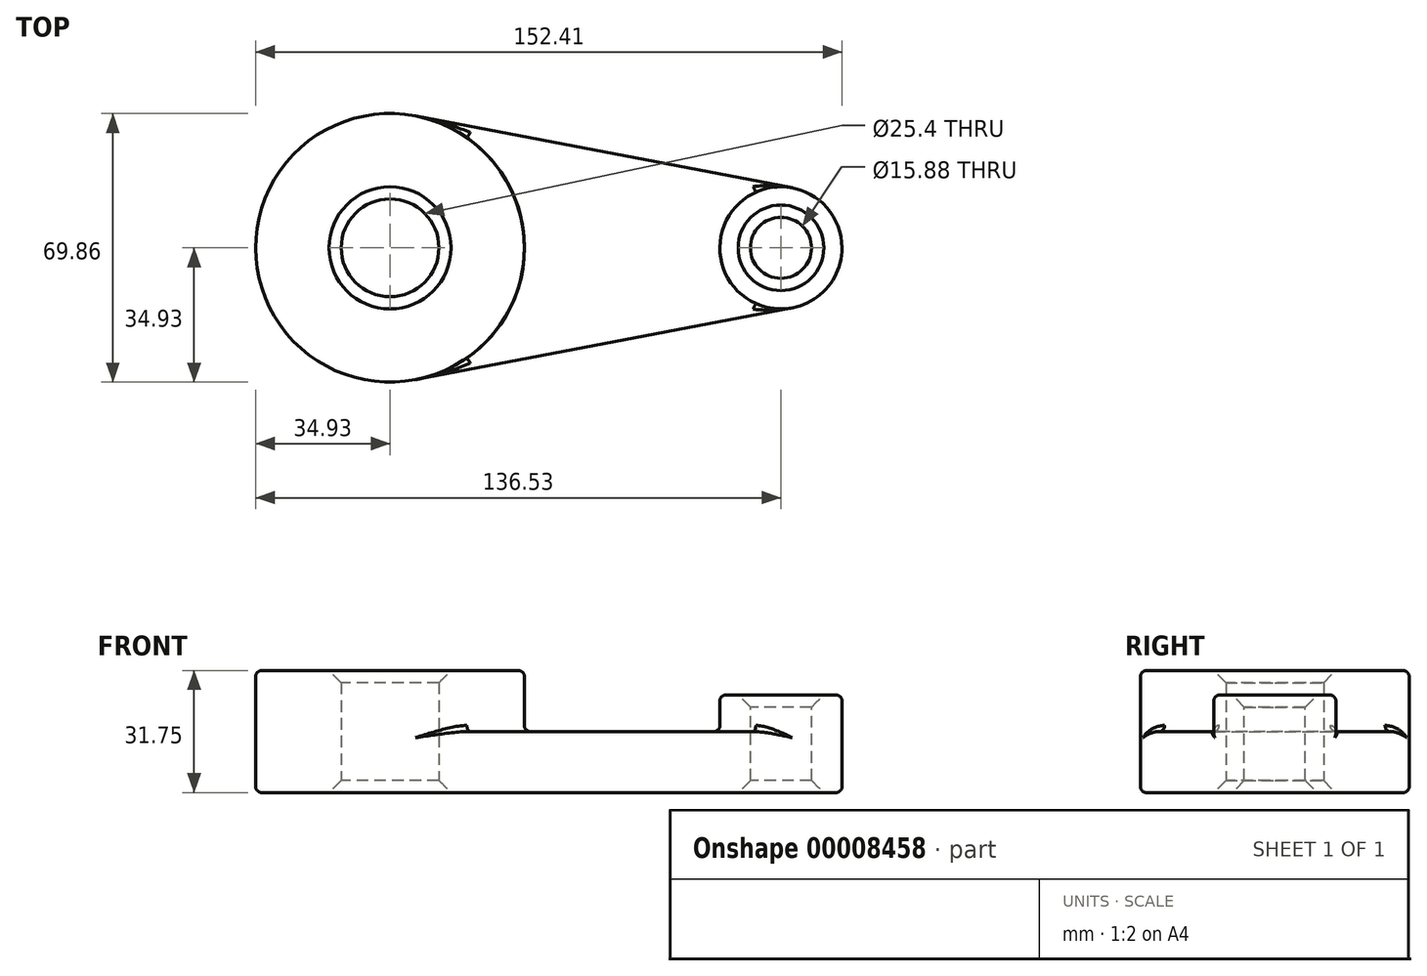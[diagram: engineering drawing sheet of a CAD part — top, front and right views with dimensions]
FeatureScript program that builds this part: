
annotation { "Feature Type Name" : "Feature", "Feature Type Description" : "" }
export const myFeature = defineFeature(function(context is Context, id is Id, definition is map)
    precondition{}
    {
        {
            var Q0;
            Q0=qCreatedBy(makeId("Top.planeOp"),FACE);
            var sketch = newSketch(context, id + "F0", { "sketchPlane" : qUnion([Q0])});
            skCircle(sketch, "E0", {"center": v(0, 0) * mm, "radius": 12.7 * mm});
            skCircle(sketch, "E1", {"center": v(0, 0) * mm, "radius": 34.93 * mm});
            skLineSegment(sketch, "E2", {"start": v(0, 0) * mm, "end": v(101.6, 0) * mm, "construction": true});
            skCircle(sketch, "E3", {"center": v(101.6, 0) * mm, "radius": 15.88 * mm});
            skLineSegment(sketch, "E4", {"start": v(6.55, 34.3) * mm, "end": v(104.58, 15.6) * mm});
            skLineSegment(sketch, "E5", {"start": v(6.55, -34.3) * mm, "end": v(104.58, -15.6) * mm});
            skSolve(sketch);
        }
        {
            var Q0;
            Q0=makeQuery(id+"F0.imprint","IMPRINT",FACE,{"disambiguationData":[TD([[makeQuery(id+"F0.imprint","IMPRINT",EDGE,{"derivedFrom":sQuery(id+"F0.wireOp",EDGE,"E0")}),-1.0]])]});
            extrude(context, id + "F1", {"entities" : qUnion([Q0]), "depth" : 31.75 * mm});
        }
        {
            var Q0;
            {var subQ1=sQuery(id+"F0.wireOp",EDGE,"E4");Q0=makeQuery(id+"F0.imprint","IMPRINT",FACE,{"disambiguationData":[TD([[makeQuery(id+"F0.imprint","IMPRINT",EDGE,{"derivedFrom":subQ1}),-1.0]])]});}
            extrude(context, id + "F2", {"entities" : qUnion([Q0]), "operationType" : NewBodyOperationType.ADD, "depth" : 15.88 * mm});
        }
        {
            var Q0;
            {var subQ0=sQuery(id+"F0.wireOp",EDGE,"E3");var subQ2=makeQuery(id+"F0.imprint","INTERSECT",VERTEX,{"derivedFrom":[subQ0,sQuery(id+"F0.wireOp",EDGE,"E4")]});Q0=makeQuery(id+"F0.imprint","IMPRINT",FACE,{"disambiguationData":[TD([[makeQuery(id+"F0.imprint","IMPRINT",EDGE,{"disambiguationData":[TD([[subQ2,-1.0]])],"derivedFrom":subQ0}),1.0]])]});}
            extrude(context, id + "F3", {"entities" : qUnion([Q0]), "operationType" : NewBodyOperationType.ADD, "depth" : 25.4 * mm});
        }
        {
            var Q0;
            Q0=makeQuery(id+"F3.opExtrude","CAP_FACE",FACE,{"disambiguationData":[OSD([sQuery(id+"F0.wireOp",EDGE,"E3")])],"isStart":false});
            var sketch = newSketch(context, id + "F4", { "sketchPlane" : qUnion([Q0])});
            skCircle(sketch, "E6", {"center": v(101.6, 0) * mm, "radius": 7.94 * mm});
            skSolve(sketch);
        }
        {
            var Q0;
            Q0=makeQuery(id+"F4.imprint","IMPRINT",FACE,{"disambiguationData":[TD([[makeQuery(id+"F4.imprint","IMPRINT",EDGE,{"derivedFrom":sQuery(id+"F4.wireOp",EDGE,"E6")}),1.0]])]});
            var Q1;
            Q1 = qSketchRegion(id + "F4", true);
            extrude(context, id + "F5", {"entities" : qUnion([Q0, Q1]), "operationType" : NewBodyOperationType.REMOVE, "endBound" : BoundingType.THROUGH_ALL, "oppositeDirection" : true, "depth" : 25.4 * mm});
        }
        {
            var Q0;
            Q0=makeQuery(id+"F2.opExtrude","CAP_FACE",FACE,{"disambiguationData":[OSD([sQuery(id+"F0.wireOp",EDGE,"E1"),sQuery(id+"F0.wireOp",EDGE,"E3"),sQuery(id+"F0.wireOp",EDGE,"E4"),sQuery(id+"F0.wireOp",EDGE,"E5")])],"isStart":false});
            var Q1;
            Q1=makeQuery(id+"F1.opExtrude","SWEPT_FACE",FACE,{"disambiguationData":[OSD([sQuery(id+"F0.wireOp",EDGE,"E1")])]});
            var Q2;
            Q2=makeQuery(id+"F3.opExtrude","SWEPT_FACE",FACE,{"disambiguationData":[OSD([sQuery(id+"F0.wireOp",EDGE,"E3")])]});
            fillet(context, id + "F6", {"entities" : qUnion([Q0, Q1, Q2]), "radius" : 1.59 * mm, "tangentPropagation" : true, "allowEdgeOverflow" : false});
        }
        {
            var Q0;
            Q0=makeQuery(id+"F1.opExtrude","SWEPT_FACE",FACE,{"disambiguationData":[OSD([sQuery(id+"F0.wireOp",EDGE,"E0")])]});
            var Q1;
            Q1=makeQuery(id+"F5.boolean.opBoolean","COPY",FACE,{"derivedFrom":makeQuery(id+"F5.opExtrude","SWEPT_FACE",FACE,{"disambiguationData":[OSD([sQuery(id+"F4.wireOp",EDGE,"E6")])]})});
            chamfer(context, id + "F7", {"entities" : qUnion([Q0, Q1]), "width" : 3.17 * mm, "tangentPropagation" : true});
        }
    });
